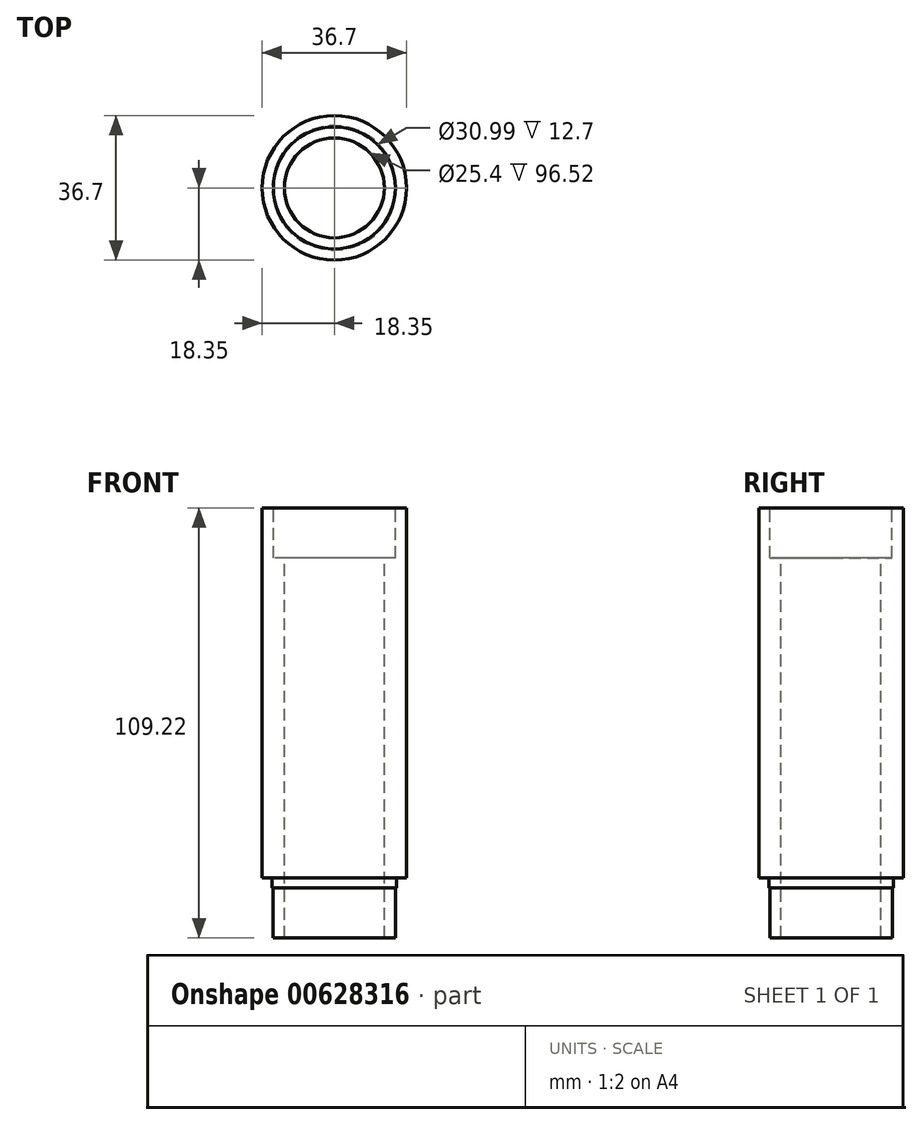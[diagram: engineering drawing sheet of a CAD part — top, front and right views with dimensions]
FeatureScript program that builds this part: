
annotation { "Feature Type Name" : "Feature", "Feature Type Description" : "" }
export const myFeature = defineFeature(function(context is Context, id is Id, definition is map)
    precondition{}
    {
        {
            var Q0;
            Q0=qCreatedBy(makeId("Front.planeOp"),FACE);
            var sketch = newSketch(context, id + "F0", { "sketchPlane" : qUnion([Q0])});
            skLineSegment(sketch, "E0", {"start": v(18.35, -64.35) * mm, "end": v(15.81, -64.35) * mm});
            skLineSegment(sketch, "E1", {"start": v(15.81, -64.35) * mm, "end": v(15.81, -66.9) * mm});
            skLineSegment(sketch, "E2.trimOffspring", {"start": v(18.35, -64.35) * mm, "end": v(18.35, 29.63) * mm});
            skLineSegment(sketch, "E3", {"start": v(18.35, 29.63) * mm, "end": v(15.5, 29.63) * mm});
            skLineSegment(sketch, "E4", {"start": v(15.5, 29.63) * mm, "end": v(15.5, 16.93) * mm});
            skLineSegment(sketch, "E5", {"start": v(15.5, 16.93) * mm, "end": v(12.7, 16.93) * mm});
            skLineSegment(sketch, "E6", {"start": v(12.7, 16.93) * mm, "end": v(12.7, -79.6) * mm});
            skLineSegment(sketch, "E7", {"start": v(12.7, -79.6) * mm, "end": v(15.56, -79.6) * mm});
            skLineSegment(sketch, "E8", {"start": v(15.56, -79.6) * mm, "end": v(15.56, -66.9) * mm});
            skLineSegment(sketch, "E9", {"start": v(15.81, -66.9) * mm, "end": v(15.56, -66.9) * mm});
            skLineSegment(sketch, "E10", {"start": v(0, 10.61) * mm, "end": v(0, -31.95) * mm});
            skSolve(sketch);
        }
        {
            var Q0;
            Q0 = qSketchRegion(id + "F0", true);
            var Q1;
            Q1=sQuery(id+"F0.wireOp",EDGE,"E10");
            revolve(context, id + "F1", {"entities" : qUnion([Q0]), "axis" : qUnion([Q1]), "revolveType" : RevolveType.FULL});
        }
    });
